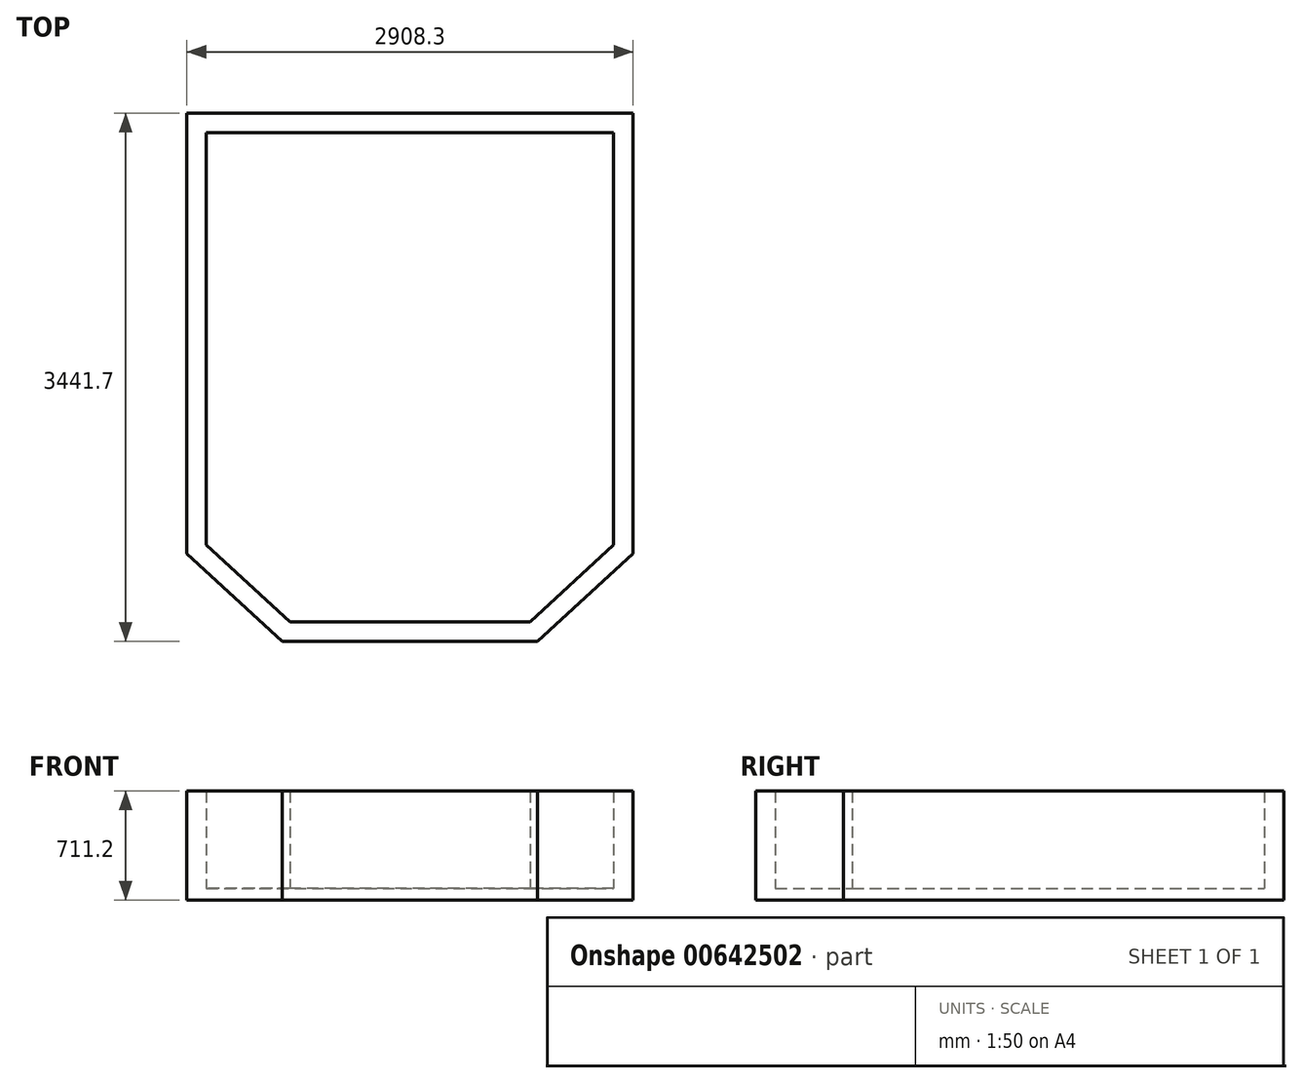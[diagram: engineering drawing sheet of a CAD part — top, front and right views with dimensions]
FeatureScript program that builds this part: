
annotation { "Feature Type Name" : "Feature", "Feature Type Description" : "" }
export const myFeature = defineFeature(function(context is Context, id is Id, definition is map)
    precondition{}
    {
        {
            var Q0;
            Q0=qCreatedBy(makeId("Top.planeOp"),FACE);
            var sketch = newSketch(context, id + "F0", { "sketchPlane" : qUnion([Q0])});
            skLineSegment(sketch, "E0", {"start": v(0, 0) * mm, "end": v(2908.3, 0) * mm});
            skLineSegment(sketch, "E1", {"start": v(2908.3, 0) * mm, "end": v(2908.3, -2870.2) * mm});
            skLineSegment(sketch, "E2", {"start": v(2908.3, -2870.2) * mm, "end": v(2286, -3441.7) * mm});
            skLineSegment(sketch, "E3", {"start": v(2286, -3441.7) * mm, "end": v(622.3, -3441.7) * mm});
            skLineSegment(sketch, "E4", {"start": v(622.3, -3441.7) * mm, "end": v(0, -2870.2) * mm});
            skLineSegment(sketch, "E5", {"start": v(0, -2870.2) * mm, "end": v(0, 0) * mm});
            skSolve(sketch);
        }
        {
            var Q0;
            Q0=makeQuery(id+"F0.imprint","IMPRINT",FACE,{"disambiguationData":[TD([[makeQuery(id+"F0.imprint","IMPRINT",EDGE,{"derivedFrom":sQuery(id+"F0.wireOp",EDGE,"E0")}),-1.0]])]});
            extrude(context, id + "F1", {"entities" : qUnion([Q0]), "depth" : 76.2 * mm, "offsetDistance" : 25.4 * mm});
        }
        {
            var Q0;
            Q0=makeQuery(id+"F1.opExtrude","CAP_FACE",FACE,{"disambiguationData":[OSD([sQuery(id+"F0.wireOp",EDGE,"E0"),sQuery(id+"F0.wireOp",EDGE,"E1"),sQuery(id+"F0.wireOp",EDGE,"E2"),sQuery(id+"F0.wireOp",EDGE,"E3"),sQuery(id+"F0.wireOp",EDGE,"E4"),sQuery(id+"F0.wireOp",EDGE,"E5")])],"isStart":false});
            var sketch = newSketch(context, id + "F2", { "sketchPlane" : qUnion([Q0])});
            skLineSegment(sketch, "E6", {"start": v(0, 0) * mm, "end": v(2908.3, 0) * mm});
            skLineSegment(sketch, "E7", {"start": v(2908.3, 0) * mm, "end": v(2908.3, -2870.2) * mm});
            skLineSegment(sketch, "E8", {"start": v(2908.3, -2870.2) * mm, "end": v(2286, -3441.7) * mm});
            skLineSegment(sketch, "E9", {"start": v(2286, -3441.7) * mm, "end": v(622.3, -3441.7) * mm});
            skLineSegment(sketch, "E10", {"start": v(622.3, -3441.7) * mm, "end": v(0, -2870.2) * mm});
            skLineSegment(sketch, "E11", {"start": v(0, -2870.2) * mm, "end": v(0, 0) * mm});
            skLineSegment(sketch, "E12", {"start": v(0, 0) * mm, "end": v(0, -2870.2) * mm});
            skLineSegment(sketch, "E13", {"start": v(622.3, -3441.7) * mm, "end": v(2286, -3441.7) * mm});
            skLineSegment(sketch, "E14", {"start": v(2908.3, -2870.2) * mm, "end": v(2908.3, 0) * mm});
            skLineSegment(sketch, "E15.0", {"start": v(671.77, -3314.7) * mm, "end": v(127, -2814.4) * mm});
            skLineSegment(sketch, "E15.1", {"start": v(127, -127) * mm, "end": v(2781.3, -127) * mm});
            skLineSegment(sketch, "E15.2", {"start": v(2781.3, -127) * mm, "end": v(2781.3, -2814.4) * mm});
            skLineSegment(sketch, "E15.3", {"start": v(127, -2814.4) * mm, "end": v(127, -127) * mm});
            skLineSegment(sketch, "E15.4", {"start": v(2781.3, -2814.4) * mm, "end": v(2236.53, -3314.7) * mm});
            skLineSegment(sketch, "E15.5", {"start": v(2236.53, -3314.7) * mm, "end": v(671.77, -3314.7) * mm});
            skSolve(sketch);
        }
        {
            var Q0;
            Q0 = qSketchRegion(id + "F2", true);
            extrude(context, id + "F3", {"entities" : qUnion([Q0]), "operationType" : NewBodyOperationType.ADD, "depth" : 635 * mm, "offsetDistance" : 25.4 * mm});
        }
    });
